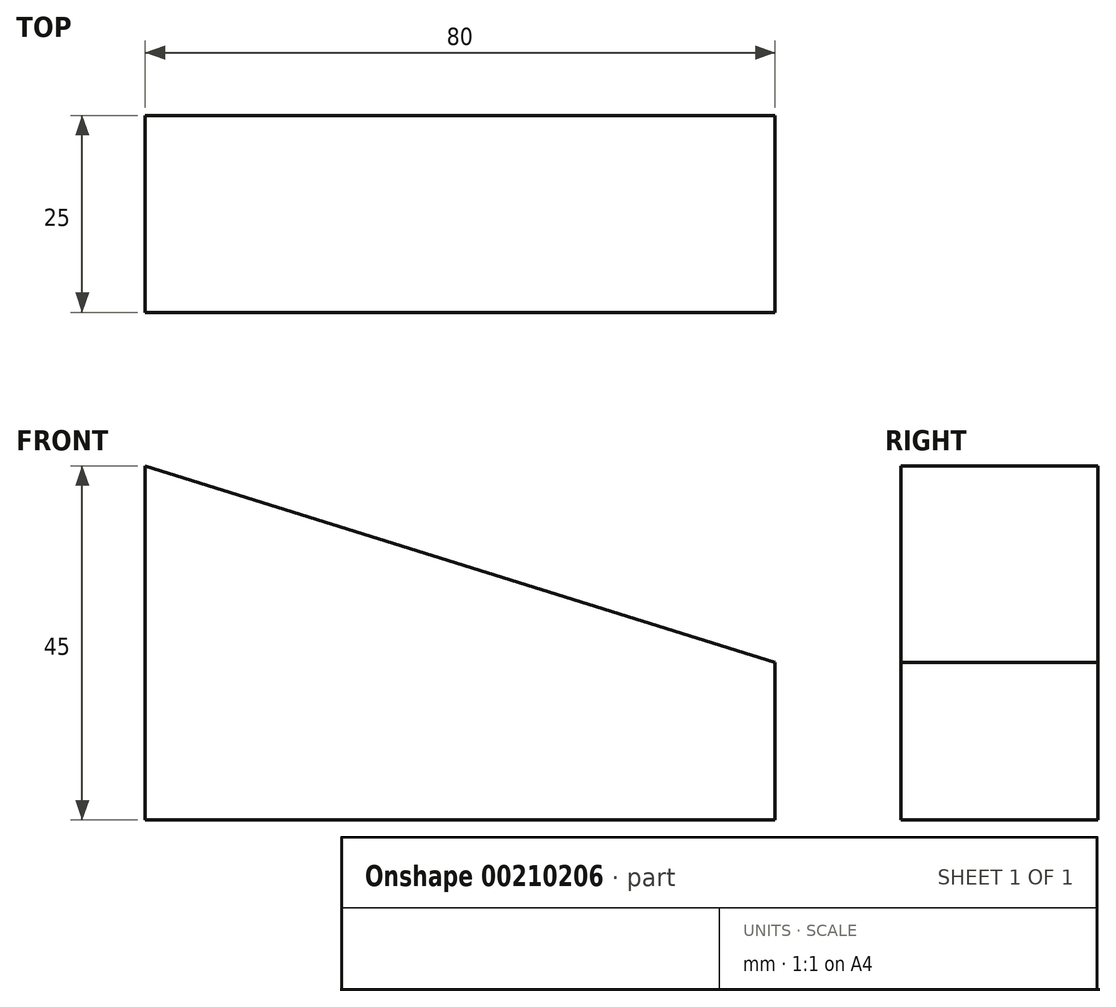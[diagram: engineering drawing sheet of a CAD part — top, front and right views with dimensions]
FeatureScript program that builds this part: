
annotation { "Feature Type Name" : "Feature", "Feature Type Description" : "" }
export const myFeature = defineFeature(function(context is Context, id is Id, definition is map)
    precondition{}
    {
        {
            var Q0;
            Q0=qCreatedBy(makeId("Front.planeOp"),FACE);
            var sketch = newSketch(context, id + "F0", { "sketchPlane" : qUnion([Q0])});
            skLineSegment(sketch, "E0", {"start": v(0, 0) * mm, "end": v(80, 0) * mm});
            skLineSegment(sketch, "E1", {"start": v(80, 0) * mm, "end": v(80, 20) * mm});
            skLineSegment(sketch, "E2", {"start": v(80, 20) * mm, "end": v(0, 45) * mm});
            skLineSegment(sketch, "E3", {"start": v(0, 45) * mm, "end": v(0, 0) * mm});
            skSolve(sketch);
        }
        {
            var Q0;
            Q0 = qSketchRegion(id + "F0", true);
            extrude(context, id + "F1", {"entities" : qUnion([Q0]), "depth" : 25 * mm});
        }
    });
